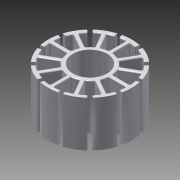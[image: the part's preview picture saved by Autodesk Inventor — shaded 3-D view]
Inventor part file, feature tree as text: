
AUTODESK INVENTOR PART (.ipt)
format: ipt  version: 2015 (Build 190159000, 159)  size: 709,120 bytes
history: native  units: in
note: dims shown in document units (in); Inventor stores cm internally (conversion verified against a paired STEP export)
features: fillet x1, other x1, imported_body x1
ambient origin geometry x8: Origin, YZ Plane, XZ Plane, XY Plane, X Axis, Y Axis, Z Axis, Center Point
bodies: Body1 (feature_tree)
feature tree (3):
  fillet  "Fillet2"  [1 undecoded]
  other  "Stator_Steelcore.ipt1"
  imported_body  "Base1"
note: 1 required parameter value undecoded (feature->parameter linkage not recoverable at this tier; creation-order binding heuristic only, values carry confidence <= 0.55)
